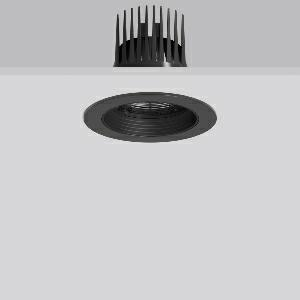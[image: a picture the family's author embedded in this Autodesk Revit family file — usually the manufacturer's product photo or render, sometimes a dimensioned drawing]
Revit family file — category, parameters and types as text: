
# Revit family: heledon_maxi_e_901775_003_2264
name_source: partatom
category: Lighting Fixtures
units: mm (PartAtom-declared; Revit-internal decimal feet)

## family parameters
Cut with Voids When Loaded = No
Host = Face
Light Source = No
Part Type = Normal
Room Calculation Point = No
Round Connector Dimension = Use Diameter
Shared = No

## types (1)
- HELEDON maxi E (1 x LED Modul 932 fresh meat, 1750 lm, 3200)
    Apparent Load = 33 VA
    Approval mark = CE
    CIE Flux Codes = 96 99 100 100 100
    Color Rendering = 90
    Color Temperature = 3200
    Default Elevation = 1800 mm
    Description = Series: HELEDON maxi
Round recessed downlight. Housing: die-cast aluminium, powder-coated. Black plastic ring and recessed LED to prevent glare from the side. Optical assembly with lens made of plastic (polycarbonate) for the best homogeneous light distribution - can be changed without tools. Special LED for illumination of meat included. Suitable for Recessed ceiling mounting. Installation without tools thanks to spring fastening system. Including separate LED converter with connecting cable 600 mm.High quality converter without flickering and stroboscopic effect. Through-wiring box (5 pole) available as accessory. The following accessories can be mounted without use of tools: interchangeable lenses, decorative glasses, honeycomb louvre, clear and frosted diffusers, white interchangeable plastic ring. 
Colour: deep black, matt (RAL 9005)
Diameter: 162 mm
Height: 3 mm
Cut-out diameter: 152 mm
Recess height: 200 mm
Luminaire: recess height: 135 mm
Lamp: LED
Socket: without socket
Colour temperature: fresh meat
System power: 33 W
Rated luminous flux: 1750 lm
Luminous efficiency: 53 lm/W
Control gear: Regulated power supply
Protection class: II
Type of protection: IP 20
    Height = 0 mm  [stored 0 ft]
    Lamp = 1 x LED Modul 932 fresh meat
    Lamp Light Flux = 1750 lm
    Lamp count = 1
    Length = 162 mm
    Lifetime = 50000 h
    Luminous efficacy = 53 lm/W
    Manufacturer = RZB
    ModVariant = No
    Model = 901775.003
    Mounting Place = Ceiling
    Mounting Type = Recessed
    Number of Poles = 1
    OnlyDefault = Yes
    Power Factor = 1
    Product Name = HELEDON maxi E
    Product group = Recessed downlights
    ProductGroupID = 402
    Protection Class = Protection class II
    Protection Degree = IP 20
    RLX_Detail_Level = 1
    RLX_Emergency_Light_Flux = 0 lm
    RLX_Emergency_Type = 0
    RLX_Emergency_Type_DB = No
    RlxData = <blob elided: 121533 chars, md5=82dc5179>
    Socket = socket
    Standby Power = 0 W
    System Light Flux = 1750 lm
    System Power = 33 W
    Type Comments = Product without accessories
    Type Image = 901663.003.jpg
    URL = http://relux.com
    VarID = ---
    Voltage = 230 V
    Voltage Range = 220-240 V
    Weight = 0.00 kg
    Width = 0 mm  [stored 0 ft]

note: [stored X ft] marks values corroborated as IEEE doubles in the binary element streams (Revit-internal decimal feet)

## geometry (parser evidence)
native form markers: Blend x4, Sweep x11
no freeform markers — native parametric forms only
